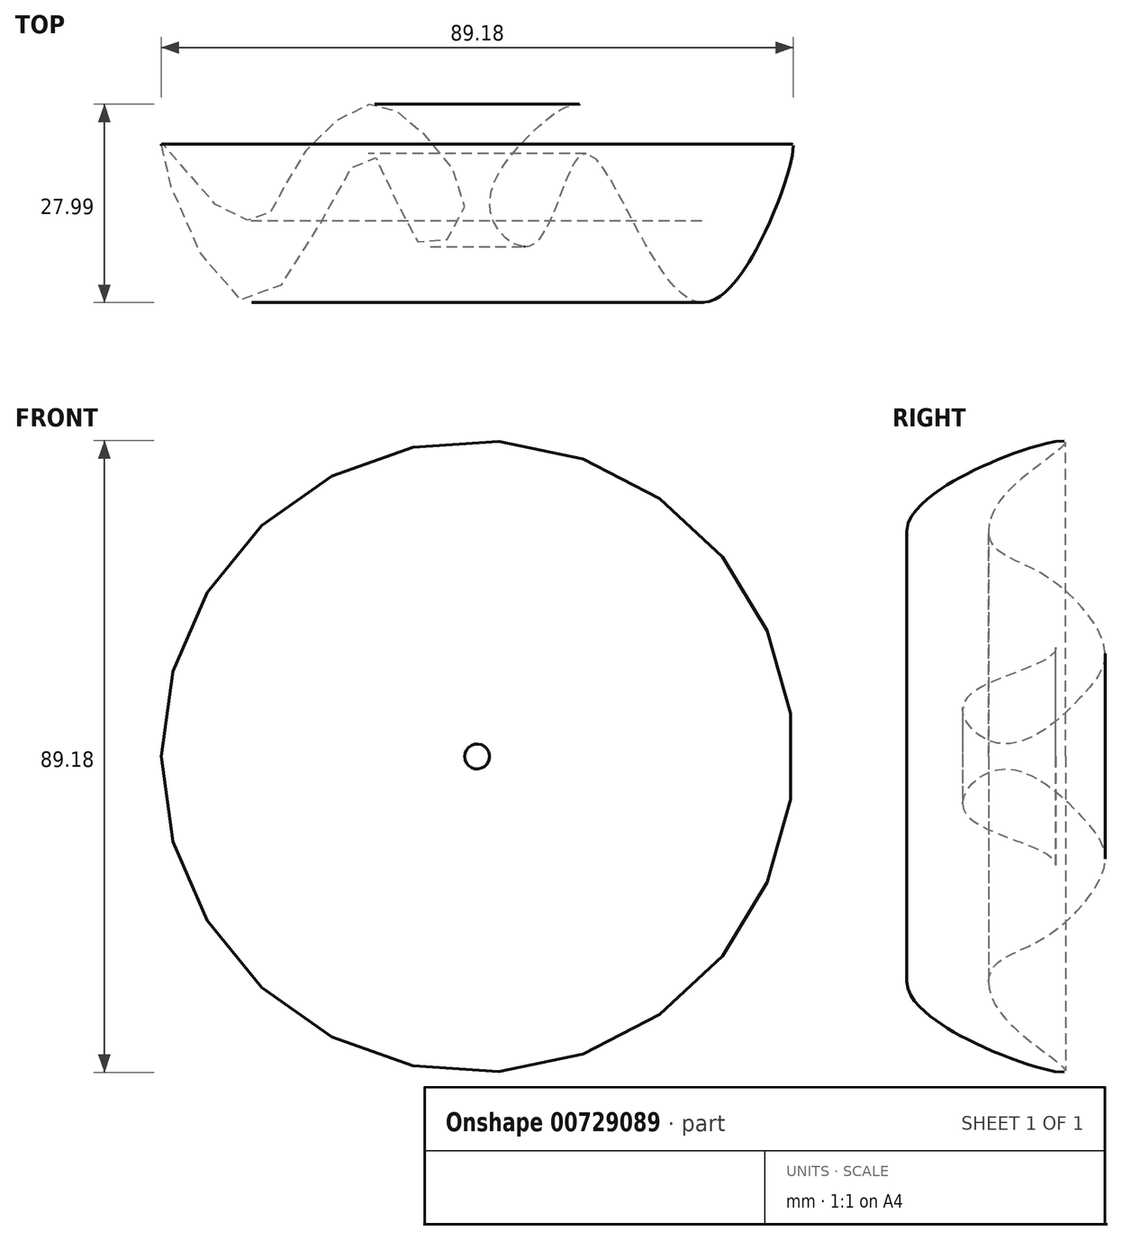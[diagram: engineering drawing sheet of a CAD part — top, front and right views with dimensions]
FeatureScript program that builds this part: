
annotation { "Feature Type Name" : "Feature", "Feature Type Description" : "" }
export const myFeature = defineFeature(function(context is Context, id is Id, definition is map)
    precondition{}
    {
        {
            var Q0;
            Q0=qCreatedBy(makeId("Top.planeOp"),FACE);
            var sketch = newSketch(context, id + "F0", { "sketchPlane" : qUnion([Q0])});
            skFitSpline(sketch, "E0", {"points": [v(-29.07, 33.4) * mm, v(-16.32, 11.2) * mm, v(0, 32.24) * mm, v(7.45, 19.53) * mm, v(13.65, 24.18) * mm, v(6.9, 35.97) * mm, v(0, 39.09) * mm, v(-10.1, 30.6) * mm, v(-14.4, 23.34) * mm, v(-21.83, 25.38) * mm, v(-29.07, 33.4) * mm]});
            skSolve(sketch);
        }
        {
            var Q0;
            Q0=qCreatedBy(makeId("Top.planeOp"),FACE);
            var sketch = newSketch(context, id + "F1", { "sketchPlane" : qUnion([Q0])});
            skLineSegment(sketch, "E1", {"start": v(15.49, 34.46) * mm, "end": v(15.49, 0) * mm});
            skSolve(sketch);
        }
        {
            var Q0;
            Q0 = qSketchRegion(id + "F1", true);
            var Q1;
            Q1=sQuery(id+"F0.wireOp",EDGE,"E0");
            var Q2;
            Q2=sQuery(id+"F1.wireOp",EDGE,"E1");
            revolve(context, id + "F2", {"bodyType" : ToolBodyType.SURFACE, "surfaceOperationType" : NewSurfaceOperationType.NEW, "entities" : qUnion([Q0]), "surfaceEntities" : qUnion([Q1]), "axis" : qUnion([Q2]), "revolveType" : RevolveType.FULL});
        }
    });
